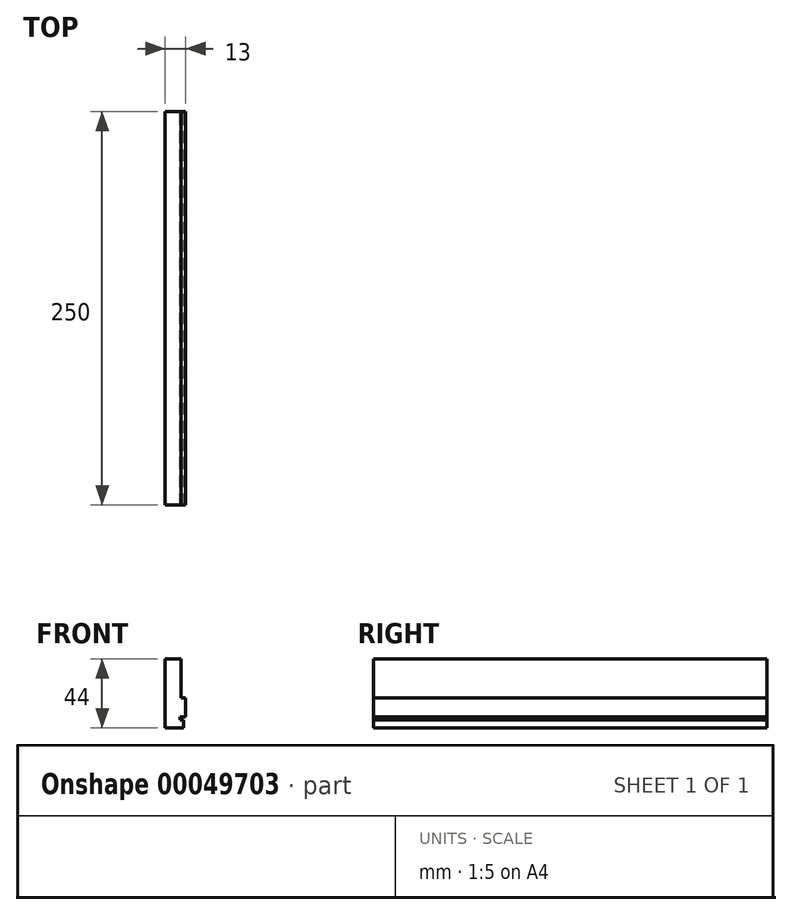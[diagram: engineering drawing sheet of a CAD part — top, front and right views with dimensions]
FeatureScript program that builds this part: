
annotation { "Feature Type Name" : "Feature", "Feature Type Description" : "" }
export const myFeature = defineFeature(function(context is Context, id is Id, definition is map)
    precondition{}
    {
        {
            var Q0;
            Q0=qCreatedBy(makeId("Front.planeOp"),FACE);
            var sketch = newSketch(context, id + "F0", { "sketchPlane" : qUnion([Q0])});
            skLineSegment(sketch, "E0", {"start": v(0, 0) * mm, "end": v(0, 12) * mm});
            skLineSegment(sketch, "E1", {"start": v(0, 12) * mm, "end": v(-3, 12) * mm});
            skLineSegment(sketch, "E2", {"start": v(-3, 12) * mm, "end": v(-3, 37) * mm});
            skLineSegment(sketch, "E3", {"start": v(-3, 37) * mm, "end": v(-13, 37) * mm});
            skLineSegment(sketch, "E4", {"start": v(-13, 37) * mm, "end": v(-13, -7) * mm});
            skLineSegment(sketch, "E5", {"start": v(-13, -7) * mm, "end": v(-1.5, -7) * mm});
            skLineSegment(sketch, "E6", {"start": v(-1.5, -7) * mm, "end": v(-1.5, -2) * mm});
            skLineSegment(sketch, "E7", {"start": v(-1.5, -2) * mm, "end": v(-3.5, -2) * mm});
            skLineSegment(sketch, "E8", {"start": v(-3.5, -2) * mm, "end": v(-3.5, 0) * mm});
            skLineSegment(sketch, "E9", {"start": v(-3.5, 0) * mm, "end": v(0.77, 0) * mm});
            skSolve(sketch);
        }
        {
            var Q0;
            Q0 = qSketchRegion(id + "F0", true);
            extrude(context, id + "F1", {"entities" : qUnion([Q0]), "depth" : 250 * mm});
        }
    });
